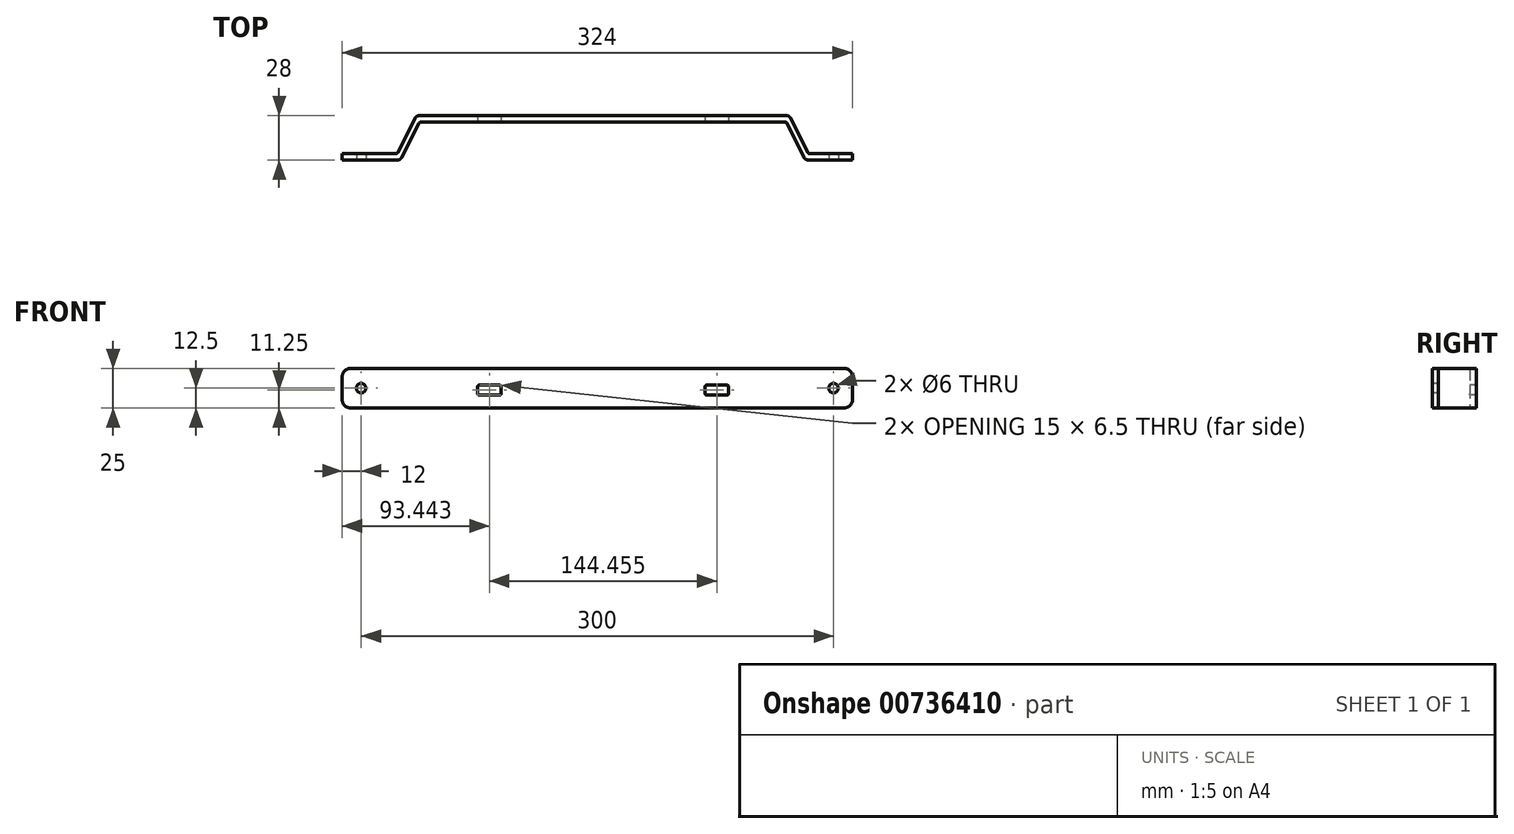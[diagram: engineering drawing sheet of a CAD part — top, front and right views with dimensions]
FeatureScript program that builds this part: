
annotation { "Feature Type Name" : "Feature", "Feature Type Description" : "" }
export const myFeature = defineFeature(function(context is Context, id is Id, definition is map)
    precondition{}
    {
        {
            var Q0;
            Q0=qCreatedBy(makeId("Top.planeOp"),FACE);
            var sketch = newSketch(context, id + "F0", { "sketchPlane" : qUnion([Q0])});
            skLineSegment(sketch, "E0.bottom", {"start": v(0, 0) * mm, "end": v(34.23, 0) * mm});
            skLineSegment(sketch, "E0.top", {"start": v(0, -4) * mm, "end": v(35.46, -4) * mm});
            skLineSegment(sketch, "E0.left", {"start": v(0, 0) * mm, "end": v(0, -4) * mm});
            skLineSegment(sketch, "E1.bottom", {"start": v(48.55, 24) * mm, "end": v(282.45, 24) * mm});
            skLineSegment(sketch, "E1.top", {"start": v(49.94, 20) * mm, "end": v(281.4, 20) * mm});
            skLineSegment(sketch, "E2.bottom", {"start": v(296.77, 0) * mm, "end": v(324, 0) * mm});
            skLineSegment(sketch, "E2.top", {"start": v(295.56, -4) * mm, "end": v(324, -4) * mm});
            skLineSegment(sketch, "E2.right", {"start": v(324, 0) * mm, "end": v(324, -4) * mm});
            skLineSegment(sketch, "E3", {"start": v(46.3, 22.62) * mm, "end": v(35.35, 0.7) * mm});
            skLineSegment(sketch, "E4", {"start": v(48.83, 19.32) * mm, "end": v(37.7, -2.63) * mm});
            skLineSegment(sketch, "E5", {"start": v(293.31, -2.6) * mm, "end": v(282.52, 19.3) * mm});
            skLineSegment(sketch, "E6", {"start": v(295.65, 0.7) * mm, "end": v(284.7, 22.62) * mm});
            skPoint(sketch, "E7.visualSharp", {"position": v(282.18, 20) * mm});
            skArc(sketch, "E7.filletArc", {"start": v(282.52, 19.3) * mm, "mid": v(282.06, 19.81) * mm, "end": v(281.4, 20) * mm});
            skPoint(sketch, "E8.visualSharp", {"position": v(296, 0) * mm});
            skArc(sketch, "E8.filletArc", {"start": v(295.65, 0.7) * mm, "mid": v(296.12, 0.19) * mm, "end": v(296.77, 0) * mm});
            skPoint(sketch, "E9.visualSharp", {"position": v(49.18, 20) * mm});
            skArc(sketch, "E9.filletArc", {"start": v(49.94, 20) * mm, "mid": v(49.29, 19.82) * mm, "end": v(48.83, 19.32) * mm});
            skPoint(sketch, "E10.visualSharp", {"position": v(35, 0) * mm});
            skArc(sketch, "E10.filletArc", {"start": v(34.23, 0) * mm, "mid": v(34.88, 0.19) * mm, "end": v(35.35, 0.7) * mm});
            skPoint(sketch, "E11.visualSharp", {"position": v(37, -4) * mm});
            skArc(sketch, "E11.filletArc", {"start": v(35.46, -4) * mm, "mid": v(36.77, -3.63) * mm, "end": v(37.7, -2.63) * mm});
            skPoint(sketch, "E12.visualSharp", {"position": v(47, 24) * mm});
            skArc(sketch, "E12.filletArc", {"start": v(48.55, 24) * mm, "mid": v(47.23, 23.63) * mm, "end": v(46.3, 22.62) * mm});
            skPoint(sketch, "E13.visualSharp", {"position": v(294, -4) * mm});
            skArc(sketch, "E13.filletArc", {"start": v(293.31, -2.6) * mm, "mid": v(294.23, -3.62) * mm, "end": v(295.56, -4) * mm});
            skPoint(sketch, "E14.visualSharp", {"position": v(284, 24) * mm});
            skArc(sketch, "E14.filletArc", {"start": v(284.7, 22.62) * mm, "mid": v(283.77, 23.63) * mm, "end": v(282.45, 24) * mm});
            skSolve(sketch);
        }
        {
            var Q0;
            Q0=qSketchRegion(id+"F0",true);
            extrude(context, id + "F1", {"entities" : qUnion([Q0]), "depth" : 25 * mm, "offsetDistance" : 25 * mm});
        }
        {
            var Q0;
            Q0=makeQuery(id+"F1.opExtrude","SWEPT_FACE",FACE,{"disambiguationData":[OSD([sQuery(id+"F0.wireOp",EDGE,"E1.top")])]});
            var sketch = newSketch(context, id + "F2", { "sketchPlane" : qUnion([Q0])});
            skLineSegment(sketch, "E15.bottom", {"start": v(87.2, 14.5) * mm, "end": v(99.7, 14.5) * mm});
            skLineSegment(sketch, "E15.top", {"start": v(87.2, 8) * mm, "end": v(99.7, 8) * mm});
            skLineSegment(sketch, "E15.left", {"start": v(85.94, 13.25) * mm, "end": v(85.94, 9.25) * mm});
            skLineSegment(sketch, "E15.right", {"start": v(100.94, 13.25) * mm, "end": v(100.94, 9.25) * mm});
            skLineSegment(sketch, "E16.bottom", {"start": v(231.65, 14.5) * mm, "end": v(244.15, 14.5) * mm});
            skLineSegment(sketch, "E16.top", {"start": v(231.65, 8) * mm, "end": v(244.15, 8) * mm});
            skLineSegment(sketch, "E16.left", {"start": v(230.4, 13.25) * mm, "end": v(230.4, 9.25) * mm});
            skLineSegment(sketch, "E16.right", {"start": v(245.4, 13.25) * mm, "end": v(245.4, 9.25) * mm});
            skPoint(sketch, "E17.visualSharp", {"position": v(245.4, 14.5) * mm});
            skArc(sketch, "E17.filletArc", {"start": v(245.4, 13.25) * mm, "mid": v(245.03, 14.13) * mm, "end": v(244.15, 14.5) * mm});
            skPoint(sketch, "E18.visualSharp", {"position": v(245.4, 8) * mm});
            skArc(sketch, "E18.filletArc", {"start": v(244.15, 8) * mm, "mid": v(245.03, 8.37) * mm, "end": v(245.4, 9.25) * mm});
            skPoint(sketch, "E19.visualSharp", {"position": v(230.4, 8) * mm});
            skArc(sketch, "E19.filletArc", {"start": v(230.4, 9.25) * mm, "mid": v(230.76, 8.37) * mm, "end": v(231.65, 8) * mm});
            skPoint(sketch, "E20.visualSharp", {"position": v(230.4, 14.5) * mm});
            skArc(sketch, "E20.filletArc", {"start": v(231.65, 14.5) * mm, "mid": v(230.76, 14.13) * mm, "end": v(230.4, 13.25) * mm});
            skPoint(sketch, "E21.visualSharp", {"position": v(85.94, 14.5) * mm});
            skArc(sketch, "E21.filletArc", {"start": v(87.2, 14.5) * mm, "mid": v(86.3, 14.13) * mm, "end": v(85.94, 13.25) * mm});
            skPoint(sketch, "E22.visualSharp", {"position": v(85.94, 8) * mm});
            skArc(sketch, "E22.filletArc", {"start": v(85.94, 9.25) * mm, "mid": v(86.3, 8.37) * mm, "end": v(87.2, 8) * mm});
            skPoint(sketch, "E23.visualSharp", {"position": v(100.94, 14.5) * mm});
            skArc(sketch, "E23.filletArc", {"start": v(100.94, 13.25) * mm, "mid": v(100.58, 14.13) * mm, "end": v(99.7, 14.5) * mm});
            skPoint(sketch, "E24.visualSharp", {"position": v(100.94, 8) * mm});
            skArc(sketch, "E24.filletArc", {"start": v(99.7, 8) * mm, "mid": v(100.58, 8.37) * mm, "end": v(100.94, 9.25) * mm});
            skSolve(sketch);
        }
        {
            var Q0;
            Q0=qSketchRegion(id+"F2",true);
            extrude(context, id + "F3", {"entities" : qUnion([Q0]), "operationType" : NewBodyOperationType.REMOVE, "oppositeDirection" : true, "depth" : 4 * mm, "offsetDistance" : 25 * mm});
        }
        {
            var Q0;
            Q0=makeQuery(id+"F1.opExtrude","CAP_EDGE",EDGE,{"disambiguationData":[OSD([sQuery(id+"F0.wireOp",EDGE,"E2.right")])],"isStart":false});
            var Q1;
            Q1=makeQuery(id+"F1.opExtrude","CAP_EDGE",EDGE,{"disambiguationData":[OSD([sQuery(id+"F0.wireOp",EDGE,"E2.right")])],"isStart":true});
            var Q2;
            Q2=makeQuery(id+"F1.opExtrude","CAP_EDGE",EDGE,{"disambiguationData":[OSD([sQuery(id+"F0.wireOp",EDGE,"E0.left")])],"isStart":false});
            var Q3;
            Q3=makeQuery(id+"F1.opExtrude","CAP_EDGE",EDGE,{"disambiguationData":[OSD([sQuery(id+"F0.wireOp",EDGE,"E0.left")])],"isStart":true});
            fillet(context, id + "F4", {"entities" : qUnion([Q0, Q1, Q2, Q3]), "radius" : 5 * mm, "tangentPropagation" : true, "allowEdgeOverflow" : false});
        }
        {
            var Q0;
            Q0=makeQuery(id+"F1.opExtrude","SWEPT_FACE",FACE,{"disambiguationData":[OSD([sQuery(id+"F0.wireOp",EDGE,"E0.top")])]});
            var sketch = newSketch(context, id + "F5", { "sketchPlane" : qUnion([Q0])});
            skCircle(sketch, "E25", {"center": v(12, 12.5) * mm, "radius": 3 * mm});
            skSolve(sketch);
        }
        {
            var Q0;
            Q0=qSketchRegion(id+"F5",true);
            extrude(context, id + "F6", {"entities" : qUnion([Q0]), "operationType" : NewBodyOperationType.REMOVE, "oppositeDirection" : true, "depth" : 4 * mm, "offsetDistance" : 25 * mm});
        }
        {
            var Q0;
            Q0=makeQuery(id+"F1.opExtrude","SWEPT_FACE",FACE,{"disambiguationData":[OSD([sQuery(id+"F0.wireOp",EDGE,"E2.top")])]});
            var sketch = newSketch(context, id + "F7", { "sketchPlane" : qUnion([Q0])});
            skCircle(sketch, "E26", {"center": v(312, 12.5) * mm, "radius": 3 * mm});
            skSolve(sketch);
        }
        {
            var Q0;
            Q0=qSketchRegion(id+"F7",true);
            extrude(context, id + "F8", {"entities" : qUnion([Q0]), "operationType" : NewBodyOperationType.REMOVE, "oppositeDirection" : true, "depth" : 4 * mm, "offsetDistance" : 25 * mm});
        }
    });
